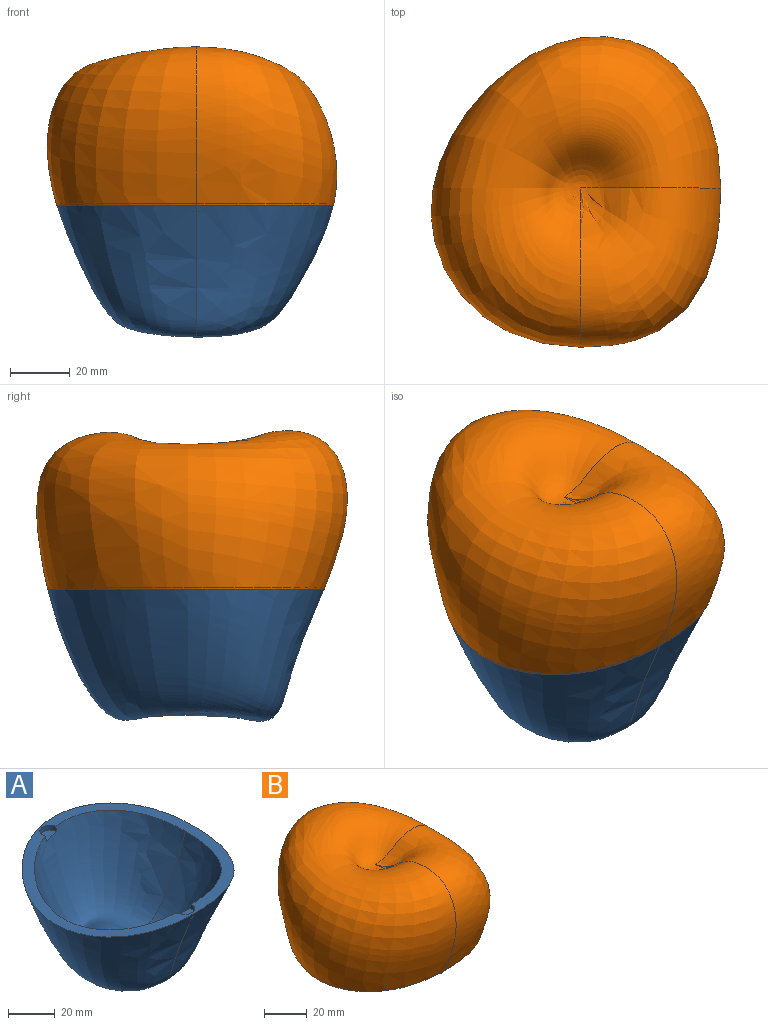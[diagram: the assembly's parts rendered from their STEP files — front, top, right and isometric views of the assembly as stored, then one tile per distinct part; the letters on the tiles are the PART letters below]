
ASSEMBLY  parts=2 mates=1
PART A: 10 faces, bbox 124.8x128.2x83.4 mm
  f0: offset ~128.17x124.84mm, area 7874.3mm2, adj f1,f2,f3,f4,f5,f6
  f1: cylinder r=4.32mm len=8.64mm, axis (0,0,1), area 37.6mm2, adj f0,f2,f3,f6
  f2: plane 8.71x5.54mm, normal (0,0,1), area 38.5mm2, adj f0,f1,f3
  f3: offset ~67.56x60.42mm, area 2707.6mm2, adj f0,f1,f2,f6
  f4: plane 8.78x6.4mm, normal (0,0,1), area 35.7mm2, adj f0,f5
  f5: cylinder r=4.32mm len=8.63mm, axis (0,0,1), area 37.4mm2, adj f0,f4,f6
  f6: plane 99.05x98.95mm, normal (0,0,1), area 1416.5mm2, adj f0,f1,f3,f5,f7,f8
  f7: bspline ~57.4x50.26mm, area 2175.3mm2, adj f6,f8
  f8: bspline ~118.01x114.68mm, area 10008.1mm2, adj f6,f7,f9
  f9: bspline ~13.38x9.5mm, area 6.6mm2, adj f8
PART B: 13 faces, bbox 125.3x132.5x90.1 mm
  f0: bspline ~122.3x115.11mm, area 15498.6mm2, adj f1,f2
  f1: bspline ~65.16x53.46mm, area 5315.8mm2, adj f0,f2
  f2: plane 92.81x92.71mm, normal (0,0,-1), area 1432.9mm2, adj f0,f1,f3,f4,f5,f7
  f3: offset ~75.32x63.62mm, area 4393.1mm2, adj f2,f4,f9,f10
  f4: offset ~132.46x125.27mm, area 12809.2mm2, adj f2,f3,f9,f10,f11,f12
  f5: cylinder r=3.81mm len=7.62mm, axis (0,0,1), area 48.6mm2, adj f2,f6,f10
  f6: plane 7.62x7.62mm, normal (0,0,-1), area 45.6mm2, adj f5
  f7: cylinder r=3.81mm len=7.62mm, axis (0,0,1), area 48.6mm2, adj f2,f8,f12
  f8: plane 7.62x7.62mm, normal (0,0,-1), area 45.6mm2, adj f7
  f9: bspline ~7.62x0.55mm, area 4.5mm2, adj f3,f4,f10
  f10: bspline ~7.62x6.91mm, area 70.8mm2, adj f3,f4,f5,f9
  f11: bspline ~7.55x4.82mm, area 2.6mm2, adj f4,f12
  f12: bspline ~7.72x7.53mm, area 64.5mm2, adj f4,f7,f11
PLACE A t=(0,0,33.02)mm
PLACE B t=(0,0,32.51)mm
MATE slider B.f5 <-> A.f1  axis (0,0,-1) through (0,-40.14,30.48)mm
